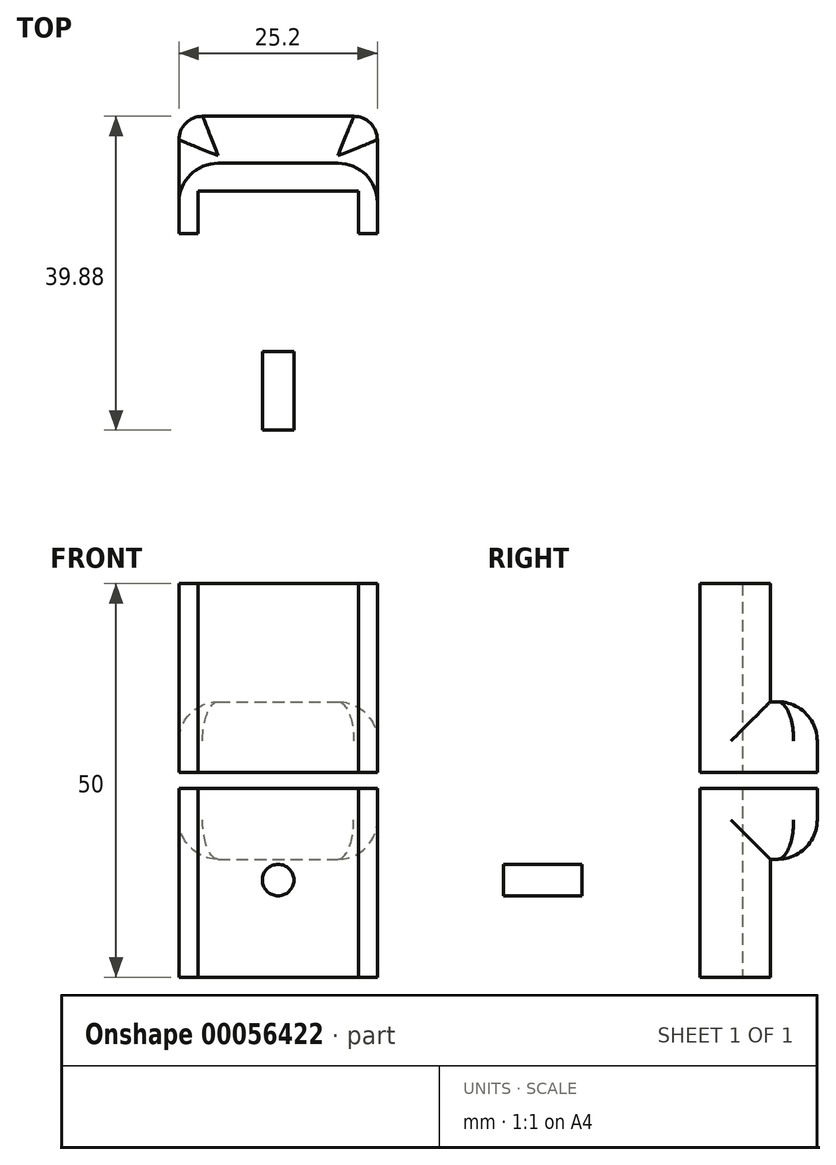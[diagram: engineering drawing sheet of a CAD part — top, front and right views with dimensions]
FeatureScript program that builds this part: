
annotation { "Feature Type Name" : "Feature", "Feature Type Description" : "" }
export const myFeature = defineFeature(function(context is Context, id is Id, definition is map)
    precondition{}
    {
        {
            var Q0;
            Q0=qCreatedBy(makeId("Top.planeOp"),FACE);
            var sketch = newSketch(context, id + "F0", { "sketchPlane" : qUnion([Q0])});
            skLineSegment(sketch, "E0.bottom", {"start": v(-53.83, -29.16) * mm, "end": v(-33.43, -29.16) * mm});
            skLineSegment(sketch, "E0.top", {"start": v(-53.83, -49.56) * mm, "end": v(-33.43, -49.56) * mm});
            skLineSegment(sketch, "E0.left", {"start": v(-53.83, -29.16) * mm, "end": v(-53.83, -49.56) * mm});
            skLineSegment(sketch, "E0.right", {"start": v(-33.43, -29.16) * mm, "end": v(-33.43, -49.56) * mm});
            skLineSegment(sketch, "E1.bottom", {"start": v(-56.23, -25.64) * mm, "end": v(-31.03, -25.64) * mm});
            skLineSegment(sketch, "E1.top", {"start": v(-56.23, -59.56) * mm, "end": v(-31.03, -59.56) * mm});
            skLineSegment(sketch, "E1.left", {"start": v(-56.23, -25.64) * mm, "end": v(-56.23, -59.56) * mm});
            skLineSegment(sketch, "E1.right", {"start": v(-31.03, -25.64) * mm, "end": v(-31.03, -59.56) * mm});
            skLineSegment(sketch, "E2", {"start": v(-56.23, -25.64) * mm, "end": v(-56.23, -22.68) * mm});
            skLineSegment(sketch, "E3", {"start": v(-53.23, -19.68) * mm, "end": v(-34.03, -19.68) * mm});
            skLineSegment(sketch, "E4", {"start": v(-31.03, -22.68) * mm, "end": v(-31.03, -25.64) * mm});
            skPoint(sketch, "E5.visualSharp", {"position": v(-56.23, -19.68) * mm});
            skArc(sketch, "E5.filletArc", {"start": v(-53.23, -19.68) * mm, "mid": v(-55.36, -20.56) * mm, "end": v(-56.23, -22.68) * mm});
            skPoint(sketch, "E6.visualSharp", {"position": v(-31.03, -19.68) * mm});
            skArc(sketch, "E6.filletArc", {"start": v(-31.03, -22.68) * mm, "mid": v(-31.91, -20.56) * mm, "end": v(-34.03, -19.68) * mm});
            skLineSegment(sketch, "E7", {"start": v(-53.83, -49.56) * mm, "end": v(-56.23, -49.56) * mm});
            skLineSegment(sketch, "E8", {"start": v(-33.43, -49.56) * mm, "end": v(-31.03, -49.56) * mm});
            skSolve(sketch);
        }
        {
            var Q0;
            Q0=makeQuery(id+"F0.imprint","IMPRINT",FACE,{"disambiguationData":[TD([[makeQuery(id+"F0.imprint","IMPRINT",EDGE,{"derivedFrom":sQuery(id+"F0.wireOp",EDGE,"E0.bottom")}),1.0]])]});
            var Q1;
            Q1=makeQuery(id+"F0.imprint","IMPRINT",FACE,{"disambiguationData":[TD([[makeQuery(id+"F0.imprint","IMPRINT",EDGE,{"derivedFrom":sQuery(id+"F0.wireOp",EDGE,"E0.top")}),-1.0]])]});
            extrude(context, id + "F1", {"entities" : qUnion([Q0, Q1]), "depth" : 50 * mm});
        }
        {
            var Q0;
            Q0=makeQuery(id+"F0.imprint","IMPRINT",FACE,{"disambiguationData":[TD([[makeQuery(id+"F0.imprint","IMPRINT",EDGE,{"derivedFrom":sQuery(id+"F0.wireOp",EDGE,"E1.bottom")}),1.0]])]});
            extrude(context, id + "F2", {"entities" : qUnion([Q0]), "operationType" : NewBodyOperationType.ADD, "depth" : 35 * mm, "hasSecondDirection" : true, "secondDirectionOppositeDirection" : false, "secondDirectionDepth" : 15 * mm});
        }
        {
            var Q0;
            Q0=makeQuery(id+"F0.imprint","IMPRINT",FACE,{"disambiguationData":[TD([[makeQuery(id+"F0.imprint","IMPRINT",EDGE,{"derivedFrom":sQuery(id+"F0.wireOp",EDGE,"E0.bottom")}),1.0]])]});
            var Q1;
            Q1=makeQuery(id+"F0.imprint","IMPRINT",FACE,{"disambiguationData":[TD([[makeQuery(id+"F0.imprint","IMPRINT",EDGE,{"derivedFrom":sQuery(id+"F0.wireOp",EDGE,"E1.bottom")}),1.0]])]});
            extrude(context, id + "F3", {"entities" : qUnion([Q0, Q1]), "operationType" : NewBodyOperationType.REMOVE, "depth" : 26 * mm, "hasSecondDirection" : true, "secondDirectionOppositeDirection" : false, "secondDirectionDepth" : 24 * mm});
        }
        {
            var Q0;
            Q0=makeQuery(id+"F2.opExtrude","CAP_EDGE",EDGE,{"disambiguationData":[OSD([sQuery(id+"F0.wireOp",EDGE,"E4")])],"isStart":false});
            var Q1;
            Q1=makeQuery(id+"F2.opExtrude","CAP_EDGE",EDGE,{"disambiguationData":[OSD([sQuery(id+"F0.wireOp",EDGE,"E6.filletArc")])],"isStart":false});
            var Q2;
            Q2=makeQuery(id+"F2.opExtrude","CAP_EDGE",EDGE,{"disambiguationData":[OSD([sQuery(id+"F0.wireOp",EDGE,"E3")])],"isStart":false});
            var Q3;
            Q3=makeQuery(id+"F2.opExtrude","CAP_EDGE",EDGE,{"disambiguationData":[OSD([sQuery(id+"F0.wireOp",EDGE,"E5.filletArc")])],"isStart":false});
            var Q4;
            Q4=makeQuery(id+"F2.opExtrude","CAP_EDGE",EDGE,{"disambiguationData":[OSD([sQuery(id+"F0.wireOp",EDGE,"E2")])],"isStart":false});
            var Q5;
            Q5=makeQuery(id+"F2.opExtrude","CAP_EDGE",EDGE,{"disambiguationData":[OSD([sQuery(id+"F0.wireOp",EDGE,"E6.filletArc")])],"isStart":true});
            var Q6;
            Q6=makeQuery(id+"F2.opExtrude","CAP_EDGE",EDGE,{"disambiguationData":[OSD([sQuery(id+"F0.wireOp",EDGE,"E3")])],"isStart":true});
            var Q7;
            Q7=makeQuery(id+"F2.opExtrude","CAP_EDGE",EDGE,{"disambiguationData":[OSD([sQuery(id+"F0.wireOp",EDGE,"E5.filletArc")])],"isStart":true});
            var Q8;
            {var subQ0=sQuery(id+"F0.wireOp",EDGE,"E4");var subQ1=sQuery(id+"F0.wireOp",EDGE,"E1.bottom");var subQ2=sQuery(id+"F0.wireOp",EDGE,"E1.right");Q8=makeQuery(id+"F2.boolean.opBoolean","SPLIT",EDGE,{"disambiguationData":[TD([makeQuery(id+"F2.opExtrude","CAP_FACE",FACE,{"disambiguationData":[OSD([subQ1,sQuery(id+"F0.wireOp",EDGE,"E2"),sQuery(id+"F0.wireOp",EDGE,"E3"),subQ0,sQuery(id+"F0.wireOp",EDGE,"E5.filletArc"),sQuery(id+"F0.wireOp",EDGE,"E6.filletArc")])],"isStart":true})])],"derivedFrom":makeQuery(id+"F1.opExtrude","SWEPT_EDGE",EDGE,{"disambiguationData":[OSD([subQ1,subQ2,subQ0])]})});}
            var Q9;
            {var subQ0=sQuery(id+"F0.wireOp",EDGE,"E4");var subQ1=sQuery(id+"F0.wireOp",EDGE,"E1.bottom");var subQ2=sQuery(id+"F0.wireOp",EDGE,"E1.right");Q9=makeQuery(id+"F2.boolean.opBoolean","SPLIT",EDGE,{"disambiguationData":[TD([makeQuery(id+"F2.opExtrude","CAP_FACE",FACE,{"disambiguationData":[OSD([subQ1,sQuery(id+"F0.wireOp",EDGE,"E2"),sQuery(id+"F0.wireOp",EDGE,"E3"),subQ0,sQuery(id+"F0.wireOp",EDGE,"E5.filletArc"),sQuery(id+"F0.wireOp",EDGE,"E6.filletArc")])],"isStart":false})])],"derivedFrom":makeQuery(id+"F1.opExtrude","SWEPT_EDGE",EDGE,{"disambiguationData":[OSD([subQ1,subQ2,subQ0])]})});}
            var Q10;
            {var subQ0=sQuery(id+"F0.wireOp",EDGE,"E2");var subQ1=sQuery(id+"F0.wireOp",EDGE,"E1.bottom");var subQ2=sQuery(id+"F0.wireOp",EDGE,"E1.left");Q10=makeQuery(id+"F2.boolean.opBoolean","SPLIT",EDGE,{"disambiguationData":[TD([makeQuery(id+"F2.opExtrude","CAP_FACE",FACE,{"disambiguationData":[OSD([subQ1,subQ0,sQuery(id+"F0.wireOp",EDGE,"E3"),sQuery(id+"F0.wireOp",EDGE,"E4"),sQuery(id+"F0.wireOp",EDGE,"E5.filletArc"),sQuery(id+"F0.wireOp",EDGE,"E6.filletArc")])],"isStart":true})])],"derivedFrom":makeQuery(id+"F1.opExtrude","SWEPT_EDGE",EDGE,{"disambiguationData":[OSD([subQ1,subQ2,subQ0])]})});}
            var Q11;
            {var subQ0=sQuery(id+"F0.wireOp",EDGE,"E2");var subQ1=sQuery(id+"F0.wireOp",EDGE,"E1.bottom");var subQ2=sQuery(id+"F0.wireOp",EDGE,"E1.left");Q11=makeQuery(id+"F2.boolean.opBoolean","SPLIT",EDGE,{"disambiguationData":[TD([makeQuery(id+"F2.opExtrude","CAP_FACE",FACE,{"disambiguationData":[OSD([subQ1,subQ0,sQuery(id+"F0.wireOp",EDGE,"E3"),sQuery(id+"F0.wireOp",EDGE,"E4"),sQuery(id+"F0.wireOp",EDGE,"E5.filletArc"),sQuery(id+"F0.wireOp",EDGE,"E6.filletArc")])],"isStart":false})])],"derivedFrom":makeQuery(id+"F1.opExtrude","SWEPT_EDGE",EDGE,{"disambiguationData":[OSD([subQ1,subQ2,subQ0])]})});}
            fillet(context, id + "F4", {"entities" : qUnion([Q0, Q1, Q2, Q3, Q4, Q5, Q6, Q7, Q8, Q9, Q10, Q11]), "radius" : 5 * mm, "tangentPropagation" : true, "allowEdgeOverflow" : false});
        }
        {
            var Q0;
            Q0=makeQuery(id+"F1.opExtrude","SWEPT_FACE",FACE,{"disambiguationData":[OSD([sQuery(id+"F0.wireOp",EDGE,"E1.top")])]});
            var sketch = newSketch(context, id + "F5", { "sketchPlane" : qUnion([Q0])});
            skLineSegment(sketch, "E9", {"start": v(-43.63, 50) * mm, "end": v(-43.63, 0) * mm, "construction": true});
            skLineSegment(sketch, "E10", {"start": v(-56.23, 25) * mm, "end": v(-31.03, 25) * mm, "construction": true});
            skCircle(sketch, "E11", {"center": v(-43.63, 37.66) * mm, "radius": 2 * mm});
            skCircle(sketch, "E12.MirrorC", {"center": v(-43.63, 12.34) * mm, "radius": 2 * mm});
            skSolve(sketch);
        }
        {
            var Q0;
            Q0=makeQuery(id+"F5.imprint","IMPRINT",FACE,{"disambiguationData":[TD([[makeQuery(id+"F5.imprint","IMPRINT",EDGE,{"derivedFrom":sQuery(id+"F5.wireOp",EDGE,"E11")}),1.0]])]});
            var Q1;
            Q1=makeQuery(id+"F5.imprint","IMPRINT",FACE,{"disambiguationData":[TD([[makeQuery(id+"F5.imprint","IMPRINT",EDGE,{"derivedFrom":sQuery(id+"F5.wireOp",EDGE,"E12.MirrorC")}),-1.0]])]});
            extrude(context, id + "F6", {"entities" : qUnion([Q0, Q1]), "operationType" : NewBodyOperationType.REMOVE, "oppositeDirection" : true, "depth" : 25 * mm});
        }
    });
